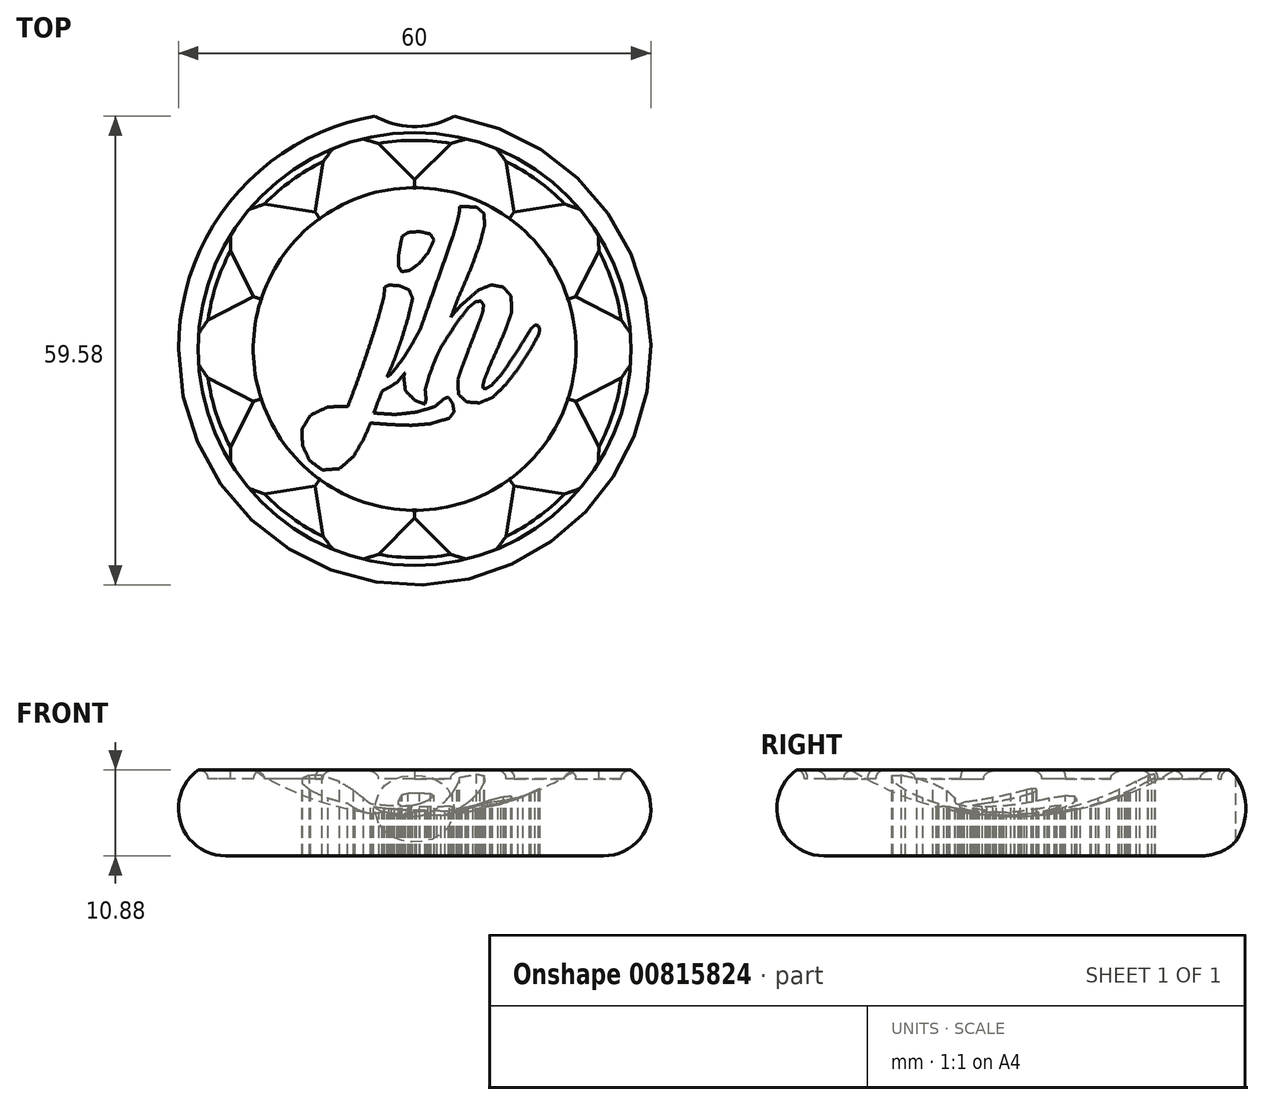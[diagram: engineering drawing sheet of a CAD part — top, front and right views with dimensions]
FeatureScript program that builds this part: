
annotation { "Feature Type Name" : "Feature", "Feature Type Description" : "" }
export const myFeature = defineFeature(function(context is Context, id is Id, definition is map)
    precondition{}
    {
        {
            var Q0;
            Q0=qCreatedBy(makeId("Front.planeOp"),FACE);
            var sketch = newSketch(context, id + "F0", { "sketchPlane" : qUnion([Q0])});
            skArc(sketch, "E0", {"start": v(-27.5, 16.42) * mm, "mid": v(-29.71, 9.7) * mm, "end": v(-24, 5.54) * mm});
            skArc(sketch, "E1", {"start": v(-20.5, 16.42) * mm, "mid": v(-10.66, 12.03) * mm, "end": v(0, 10.54) * mm});
            skLineSegment(sketch, "E2", {"start": v(-24, 5.54) * mm, "end": v(0, 5.54) * mm});
            skLineSegment(sketch, "E3", {"start": v(0, 5.54) * mm, "end": v(0, 10.54) * mm});
            skLineSegment(sketch, "E4.top", {"start": v(-27.5, 16.42) * mm, "end": v(-20.5, 16.42) * mm});
            skSolve(sketch);
        }
        {
            var Q0;
            Q0=makeQuery(id+"F0.imprint","IMPRINT",FACE,{"disambiguationData":[TD([[makeQuery(id+"F0.imprint","IMPRINT",EDGE,{"derivedFrom":sQuery(id+"F0.wireOp",EDGE,"E0")}),1.0]])]});
            var Q1;
            Q1=sQuery(id+"F0.wireOp",EDGE,"E3");
            revolve(context, id + "F1", {"surfaceOperationType" : NewSurfaceOperationType.NEW, "entities" : qUnion([Q0]), "axis" : qUnion([Q1]), "revolveType" : RevolveType.FULL});
        }
        {
            var Q0;
            Q0=qCreatedBy(makeId("Top.planeOp"),FACE);
            var Q1;
            Q1 = qBodyType(qCreatedBy(id + "F3" ,EDGE), BodyType.WIRE);
            cPlane(context, id + "F2", {"entities" : qUnion([Q0, Q1]), "cplaneType" : CPlaneType.OFFSET, "offset" : 25 * mm, "width" : 150 * mm, "height" : 150 * mm});
        }
        {
            var Q0;
            Q0=qCreatedBy(id+"F2.planeOp",FACE);
            var sketch = newSketch(context, id + "F3", { "sketchPlane" : qUnion([Q0])});
            skCircle(sketch, "E5", {"center": v(0, 0) * mm, "radius": 26.5 * mm});
            skCircle(sketch, "E6", {"center": v(0, 0) * mm, "radius": 21.5 * mm});
            skLineSegment(sketch, "E7", {"start": v(0, 21.5) * mm, "end": v(4.6, 26.1) * mm});
            skLineSegment(sketch, "E8.MirrorCS", {"start": v(0, 21.5) * mm, "end": v(-4.6, 26.1) * mm});
            skLineSegment(sketch, "E9.1.0", {"start": v(-12.64, 17.4) * mm, "end": v(-11.62, 23.82) * mm});
            skLineSegment(sketch, "E9.1.1", {"start": v(-12.64, 17.4) * mm, "end": v(-19.06, 18.41) * mm});
            skLineSegment(sketch, "E9.2.0", {"start": v(-20.45, 6.64) * mm, "end": v(-23.4, 12.44) * mm});
            skLineSegment(sketch, "E9.2.1", {"start": v(-20.45, 6.64) * mm, "end": v(-26.24, 3.7) * mm});
            skLineSegment(sketch, "E9.3.0", {"start": v(-20.45, -6.64) * mm, "end": v(-26.24, -3.7) * mm});
            skLineSegment(sketch, "E9.3.1", {"start": v(-20.45, -6.64) * mm, "end": v(-23.4, -12.44) * mm});
            skLineSegment(sketch, "E9.4.0", {"start": v(-12.64, -17.4) * mm, "end": v(-19.06, -18.41) * mm});
            skLineSegment(sketch, "E9.4.1", {"start": v(-12.64, -17.4) * mm, "end": v(-11.62, -23.82) * mm});
            skLineSegment(sketch, "E9.5.0", {"start": v(0, -21.5) * mm, "end": v(-4.6, -26.1) * mm});
            skLineSegment(sketch, "E9.5.1", {"start": v(0, -21.5) * mm, "end": v(4.6, -26.1) * mm});
            skLineSegment(sketch, "E9.6.0", {"start": v(12.64, -17.4) * mm, "end": v(11.62, -23.82) * mm});
            skLineSegment(sketch, "E9.6.1", {"start": v(12.64, -17.4) * mm, "end": v(19.06, -18.41) * mm});
            skLineSegment(sketch, "E9.7.0", {"start": v(20.45, -6.64) * mm, "end": v(23.4, -12.44) * mm});
            skLineSegment(sketch, "E9.7.1", {"start": v(20.45, -6.64) * mm, "end": v(26.24, -3.7) * mm});
            skLineSegment(sketch, "E9.8.0", {"start": v(20.45, 6.64) * mm, "end": v(26.24, 3.7) * mm});
            skLineSegment(sketch, "E9.8.1", {"start": v(20.45, 6.64) * mm, "end": v(23.4, 12.44) * mm});
            skLineSegment(sketch, "E9.9.0", {"start": v(12.64, 17.4) * mm, "end": v(19.06, 18.41) * mm});
            skLineSegment(sketch, "E9.9.1", {"start": v(12.64, 17.4) * mm, "end": v(11.62, 23.82) * mm});
            skSolve(sketch);
        }
        {
            var Q0;
            {var subQ0=sQuery(id+"F3.wireOp",EDGE,"E9.1.0");Q0=makeQuery(id+"F3.imprint","IMPRINT",FACE,{"disambiguationData":[TD([[makeQuery(id+"F3.imprint","IMPRINT",EDGE,{"derivedFrom":subQ0}),1.0]])]});}
            var Q1;
            {var subQ0=sQuery(id+"F3.wireOp",EDGE,"E7");Q1=makeQuery(id+"F3.imprint","IMPRINT",FACE,{"disambiguationData":[TD([[makeQuery(id+"F3.imprint","IMPRINT",EDGE,{"derivedFrom":subQ0}),1.0]])]});}
            var Q2;
            {var subQ0=sQuery(id+"F3.wireOp",EDGE,"E9.9.0");Q2=makeQuery(id+"F3.imprint","IMPRINT",FACE,{"disambiguationData":[TD([[makeQuery(id+"F3.imprint","IMPRINT",EDGE,{"derivedFrom":subQ0}),1.0]])]});}
            var Q3;
            {var subQ0=sQuery(id+"F3.wireOp",EDGE,"E9.8.0");Q3=makeQuery(id+"F3.imprint","IMPRINT",FACE,{"disambiguationData":[TD([[makeQuery(id+"F3.imprint","IMPRINT",EDGE,{"derivedFrom":subQ0}),1.0]])]});}
            var Q4;
            {var subQ0=sQuery(id+"F3.wireOp",EDGE,"E9.7.0");Q4=makeQuery(id+"F3.imprint","IMPRINT",FACE,{"disambiguationData":[TD([[makeQuery(id+"F3.imprint","IMPRINT",EDGE,{"derivedFrom":subQ0}),1.0]])]});}
            var Q5;
            {var subQ0=sQuery(id+"F3.wireOp",EDGE,"E9.6.0");Q5=makeQuery(id+"F3.imprint","IMPRINT",FACE,{"disambiguationData":[TD([[makeQuery(id+"F3.imprint","IMPRINT",EDGE,{"derivedFrom":subQ0}),1.0]])]});}
            var Q6;
            {var subQ0=sQuery(id+"F3.wireOp",EDGE,"E9.5.0");Q6=makeQuery(id+"F3.imprint","IMPRINT",FACE,{"disambiguationData":[TD([[makeQuery(id+"F3.imprint","IMPRINT",EDGE,{"derivedFrom":subQ0}),1.0]])]});}
            var Q7;
            {var subQ0=sQuery(id+"F3.wireOp",EDGE,"E9.4.0");Q7=makeQuery(id+"F3.imprint","IMPRINT",FACE,{"disambiguationData":[TD([[makeQuery(id+"F3.imprint","IMPRINT",EDGE,{"derivedFrom":subQ0}),1.0]])]});}
            var Q8;
            {var subQ0=sQuery(id+"F3.wireOp",EDGE,"E9.3.0");Q8=makeQuery(id+"F3.imprint","IMPRINT",FACE,{"disambiguationData":[TD([[makeQuery(id+"F3.imprint","IMPRINT",EDGE,{"derivedFrom":subQ0}),1.0]])]});}
            var Q9;
            {var subQ0=sQuery(id+"F3.wireOp",EDGE,"E9.2.0");Q9=makeQuery(id+"F3.imprint","IMPRINT",FACE,{"disambiguationData":[TD([[makeQuery(id+"F3.imprint","IMPRINT",EDGE,{"derivedFrom":subQ0}),1.0]])]});}
            extrude(context, id + "F4", {"entities" : qUnion([Q0, Q1, Q2, Q3, Q4, Q5, Q6, Q7, Q8, Q9]), "operationType" : NewBodyOperationType.REMOVE, "oppositeDirection" : true, "depth" : 9.7 * mm, "offsetDistance" : 25 * mm});
        }
        {
            var Q0;
            Q0=qCreatedBy(makeId("Top.planeOp"),FACE);
            var sketch = newSketch(context, id + "F5", { "sketchPlane" : qUnion([Q0])});
            skCircle(sketch, "E10", {"center": v(0, 38.24) * mm, "radius": 10 * mm});
            skSolve(sketch);
        }
        {
            var Q0;
            Q0=makeQuery(id+"F5.imprint","IMPRINT",FACE,{"disambiguationData":[TD([[makeQuery(id+"F5.imprint","IMPRINT",EDGE,{"derivedFrom":sQuery(id+"F5.wireOp",EDGE,"E10")}),1.0]])]});
            extrude(context, id + "F6", {"entities" : qUnion([Q0]), "operationType" : NewBodyOperationType.REMOVE, "depth" : 51 * mm, "offsetDistance" : 25 * mm});
        }
        {
            var Q0;
            Q0=qCreatedBy(id+"F2.planeOp",FACE);
            cPlane(context, id + "F7", {"entities" : qUnion([Q0]), "cplaneType" : CPlaneType.OFFSET, "offset" : 25 * mm, "width" : 150 * mm, "height" : 150 * mm});
        }
        {
            var Q0;
            Q0=qCreatedBy(id+"F7.planeOp",FACE);
            var sketch = newSketch(context, id + "F8", { "sketchPlane" : qUnion([Q0])});
            skLineSegment(sketch, "E11", {"start": v(-0.26, 6.42) * mm, "end": v(-0.82, 4) * mm});
            skLineSegment(sketch, "E12", {"start": v(-0.82, 4) * mm, "end": v(-1.68, 1.15) * mm});
            skLineSegment(sketch, "E13", {"start": v(-1.68, 1.15) * mm, "end": v(-2.63, -1.54) * mm});
            skLineSegment(sketch, "E14", {"start": v(-2.63, -1.54) * mm, "end": v(-3.47, -3.48) * mm});
            skLineSegment(sketch, "E15", {"start": v(-3.47, -3.48) * mm, "end": v(-3.1, -3.3) * mm});
            skLineSegment(sketch, "E16", {"start": v(-3.1, -3.3) * mm, "end": v(-2.7, -2.85) * mm});
            skLineSegment(sketch, "E17", {"start": v(-2.7, -2.85) * mm, "end": v(-1.4, -1.1) * mm});
            skLineSegment(sketch, "E18", {"start": v(-1.4, -1.1) * mm, "end": v(-0.26, 0.72) * mm});
            skLineSegment(sketch, "E19", {"start": v(-0.26, 0.72) * mm, "end": v(0.64, 2.37) * mm});
            skLineSegment(sketch, "E20", {"start": v(0.64, 2.37) * mm, "end": v(1.28, 3.62) * mm});
            skLineSegment(sketch, "E21", {"start": v(1.28, 3.62) * mm, "end": v(1.84, 4.39) * mm});
            skLineSegment(sketch, "E22", {"start": v(1.84, 4.39) * mm, "end": v(2.32, 4.39) * mm});
            skLineSegment(sketch, "E23", {"start": v(2.32, 4.39) * mm, "end": v(2.48, 3.73) * mm});
            skLineSegment(sketch, "E24", {"start": v(2.48, 3.73) * mm, "end": v(2.14, 2.58) * mm});
            skLineSegment(sketch, "E25", {"start": v(2.14, 2.58) * mm, "end": v(1, 0.38) * mm});
            skLineSegment(sketch, "E26", {"start": v(1, 0.38) * mm, "end": v(-0.49, -2.13) * mm});
            skLineSegment(sketch, "E27", {"start": v(-0.49, -2.13) * mm, "end": v(-2.25, -4.27) * mm});
            skLineSegment(sketch, "E28", {"start": v(-2.25, -4.27) * mm, "end": v(-4.15, -5.38) * mm});
            skLineSegment(sketch, "E29", {"start": v(-4.15, -5.38) * mm, "end": v(-5.19, -8.14) * mm});
            skLineSegment(sketch, "E30", {"start": v(-5.19, -8.14) * mm, "end": v(-2.52, -8.32) * mm});
            skLineSegment(sketch, "E31", {"start": v(-2.52, -8.32) * mm, "end": v(0.24, -8.03) * mm});
            skLineSegment(sketch, "E32", {"start": v(0.24, -8.03) * mm, "end": v(2.54, -7.33) * mm});
            skLineSegment(sketch, "E33", {"start": v(2.54, -7.33) * mm, "end": v(3.85, -6.24) * mm});
            skLineSegment(sketch, "E34", {"start": v(3.85, -6.24) * mm, "end": v(4.3, -6.15) * mm});
            skLineSegment(sketch, "E35", {"start": v(4.3, -6.15) * mm, "end": v(4.83, -6.92) * mm});
            skLineSegment(sketch, "E36", {"start": v(4.83, -6.92) * mm, "end": v(5, -7.98) * mm});
            skLineSegment(sketch, "E37", {"start": v(5, -7.98) * mm, "end": v(4.44, -8.77) * mm});
            skLineSegment(sketch, "E38", {"start": v(4.44, -8.77) * mm, "end": v(2.07, -9.5) * mm});
            skLineSegment(sketch, "E39", {"start": v(2.07, -9.5) * mm, "end": v(-0.4, -9.7) * mm});
            skLineSegment(sketch, "E40", {"start": v(-0.4, -9.7) * mm, "end": v(-2.95, -9.6) * mm});
            skLineSegment(sketch, "E41", {"start": v(-2.95, -9.6) * mm, "end": v(-5.6, -9.4) * mm});
            skLineSegment(sketch, "E42", {"start": v(-5.6, -9.4) * mm, "end": v(-6.45, -11.42) * mm});
            skLineSegment(sketch, "E43", {"start": v(-6.45, -11.42) * mm, "end": v(-7.77, -13.63) * mm});
            skLineSegment(sketch, "E44", {"start": v(-7.77, -13.63) * mm, "end": v(-9.53, -15.22) * mm});
            skLineSegment(sketch, "E45", {"start": v(-9.53, -15.22) * mm, "end": v(-11.74, -15.37) * mm});
            skLineSegment(sketch, "E46", {"start": v(-11.74, -15.37) * mm, "end": v(-13.35, -14.15) * mm});
            skLineSegment(sketch, "E47", {"start": v(-13.35, -14.15) * mm, "end": v(-14.25, -12.2) * mm});
            skLineSegment(sketch, "E48", {"start": v(-14.25, -12.2) * mm, "end": v(-14.28, -10.13) * mm});
            skLineSegment(sketch, "E49", {"start": v(-14.28, -10.13) * mm, "end": v(-13.24, -8.41) * mm});
            skLineSegment(sketch, "E50", {"start": v(-13.24, -8.41) * mm, "end": v(-11, -7.35) * mm});
            skLineSegment(sketch, "E51", {"start": v(-11, -7.35) * mm, "end": v(-8.49, -7.33) * mm});
            skLineSegment(sketch, "E52", {"start": v(-8.49, -7.33) * mm, "end": v(-7.54, -4.82) * mm});
            skLineSegment(sketch, "E53", {"start": v(-7.54, -4.82) * mm, "end": v(-6.45, -1.74) * mm});
            skLineSegment(sketch, "E54", {"start": v(-6.45, -1.74) * mm, "end": v(-5.4, 1.47) * mm});
            skLineSegment(sketch, "E55", {"start": v(-5.4, 1.47) * mm, "end": v(-4.49, 4.4) * mm});
            skLineSegment(sketch, "E56", {"start": v(-4.49, 4.4) * mm, "end": v(-3.9, 6.67) * mm});
            skLineSegment(sketch, "E57", {"start": v(-3.9, 6.67) * mm, "end": v(-3.79, 7.87) * mm});
            skLineSegment(sketch, "E58", {"start": v(-3.79, 7.87) * mm, "end": v(-3.27, 8.12) * mm});
            skLineSegment(sketch, "E59", {"start": v(-3.27, 8.12) * mm, "end": v(-1.96, 8.05) * mm});
            skLineSegment(sketch, "E60", {"start": v(-1.96, 8.05) * mm, "end": v(-0.69, 7.5) * mm});
            skLineSegment(sketch, "E61", {"start": v(-0.69, 7.5) * mm, "end": v(-0.26, 6.42) * mm});
            skLineSegment(sketch, "E62", {"start": v(-12.2, -9.22) * mm, "end": v(-12.97, -10.6) * mm});
            skLineSegment(sketch, "E63", {"start": v(-12.97, -10.6) * mm, "end": v(-12.97, -11.87) * mm});
            skLineSegment(sketch, "E64", {"start": v(-12.97, -11.87) * mm, "end": v(-12.54, -12.8) * mm});
            skLineSegment(sketch, "E65", {"start": v(-12.54, -12.8) * mm, "end": v(-11.97, -13.2) * mm});
            skLineSegment(sketch, "E66", {"start": v(-11.97, -13.2) * mm, "end": v(-11.5, -13.23) * mm});
            skLineSegment(sketch, "E67", {"start": v(-11.5, -13.23) * mm, "end": v(-10.9, -12.8) * mm});
            skLineSegment(sketch, "E68", {"start": v(-10.9, -12.8) * mm, "end": v(-10.1, -11.42) * mm});
            skLineSegment(sketch, "E69", {"start": v(-10.1, -11.42) * mm, "end": v(-8.94, -8.55) * mm});
            skLineSegment(sketch, "E70", {"start": v(-8.94, -8.55) * mm, "end": v(-11, -8.6) * mm});
            skLineSegment(sketch, "E71", {"start": v(-11, -8.6) * mm, "end": v(-12.2, -9.22) * mm});
            skLineSegment(sketch, "E72", {"start": v(-1.57, 14.33) * mm, "end": v(-0.8, 14.8) * mm});
            skLineSegment(sketch, "E73", {"start": v(-0.8, 14.8) * mm, "end": v(0.64, 14.92) * mm});
            skLineSegment(sketch, "E74", {"start": v(0.64, 14.92) * mm, "end": v(2, 14.6) * mm});
            skLineSegment(sketch, "E75", {"start": v(2, 14.6) * mm, "end": v(2.45, 13.84) * mm});
            skLineSegment(sketch, "E76", {"start": v(2.45, 13.84) * mm, "end": v(1.73, 12.25) * mm});
            skLineSegment(sketch, "E77", {"start": v(1.73, 12.25) * mm, "end": v(0.62, 10.9) * mm});
            skLineSegment(sketch, "E78", {"start": v(0.62, 10.9) * mm, "end": v(-0.6, 10) * mm});
            skLineSegment(sketch, "E79", {"start": v(-0.6, 10) * mm, "end": v(-1.66, 9.81) * mm});
            skLineSegment(sketch, "E80", {"start": v(-1.66, 9.81) * mm, "end": v(-2.07, 10.54) * mm});
            skLineSegment(sketch, "E81", {"start": v(-2.07, 10.54) * mm, "end": v(-2.02, 11.94) * mm});
            skLineSegment(sketch, "E82", {"start": v(-2.02, 11.94) * mm, "end": v(-1.77, 13.4) * mm});
            skLineSegment(sketch, "E83", {"start": v(-1.77, 13.4) * mm, "end": v(-1.57, 14.33) * mm});
            skLineSegment(sketch, "E84", {"start": v(8.33, 13.52) * mm, "end": v(7.4, 10.87) * mm});
            skLineSegment(sketch, "E85", {"start": v(7.4, 10.87) * mm, "end": v(6.45, 8.57) * mm});
            skLineSegment(sketch, "E86", {"start": v(6.45, 8.57) * mm, "end": v(5.5, 6.38) * mm});
            skLineSegment(sketch, "E87", {"start": v(5.5, 6.38) * mm, "end": v(4.62, 4.07) * mm});
            skLineSegment(sketch, "E88", {"start": v(4.62, 4.07) * mm, "end": v(5.78, 5.45) * mm});
            skLineSegment(sketch, "E89", {"start": v(5.78, 5.45) * mm, "end": v(8.15, 7.5) * mm});
            skLineSegment(sketch, "E90", {"start": v(8.15, 7.5) * mm, "end": v(9.73, 8.14) * mm});
            skLineSegment(sketch, "E91", {"start": v(9.73, 8.14) * mm, "end": v(11.27, 7.87) * mm});
            skLineSegment(sketch, "E92", {"start": v(11.27, 7.87) * mm, "end": v(12.26, 6.7) * mm});
            skLineSegment(sketch, "E93", {"start": v(12.26, 6.7) * mm, "end": v(12.3, 4.66) * mm});
            skLineSegment(sketch, "E94", {"start": v(12.3, 4.66) * mm, "end": v(11.6, 2.58) * mm});
            skLineSegment(sketch, "E95", {"start": v(11.6, 2.58) * mm, "end": v(10.6, 0.2) * mm});
            skLineSegment(sketch, "E96", {"start": v(10.6, 0.2) * mm, "end": v(9.57, -2.08) * mm});
            skLineSegment(sketch, "E97", {"start": v(9.57, -2.08) * mm, "end": v(8.87, -3.84) * mm});
            skLineSegment(sketch, "E98", {"start": v(8.87, -3.84) * mm, "end": v(8.7, -4.52) * mm});
            skLineSegment(sketch, "E99", {"start": v(8.7, -4.52) * mm, "end": v(8.71, -4.97) * mm});
            skLineSegment(sketch, "E100", {"start": v(8.71, -4.97) * mm, "end": v(9.03, -5.06) * mm});
            skLineSegment(sketch, "E101", {"start": v(9.03, -5.06) * mm, "end": v(9.78, -4.61) * mm});
            skLineSegment(sketch, "E102", {"start": v(9.78, -4.61) * mm, "end": v(10.95, -3.3) * mm});
            skLineSegment(sketch, "E103", {"start": v(10.95, -3.3) * mm, "end": v(12.4, -1.24) * mm});
            skLineSegment(sketch, "E104", {"start": v(12.4, -1.24) * mm, "end": v(13.78, 0.93) * mm});
            skLineSegment(sketch, "E105", {"start": v(13.78, 0.93) * mm, "end": v(14.8, 2.58) * mm});
            skLineSegment(sketch, "E106", {"start": v(14.8, 2.58) * mm, "end": v(15.32, 3.05) * mm});
            skLineSegment(sketch, "E107", {"start": v(15.32, 3.05) * mm, "end": v(15.72, 2.96) * mm});
            skLineSegment(sketch, "E108", {"start": v(15.72, 2.96) * mm, "end": v(15.9, 2.49) * mm});
            skLineSegment(sketch, "E109", {"start": v(15.9, 2.49) * mm, "end": v(15.75, 1.8) * mm});
            skLineSegment(sketch, "E110", {"start": v(15.75, 1.8) * mm, "end": v(14.62, -0.25) * mm});
            skLineSegment(sketch, "E111", {"start": v(14.62, -0.25) * mm, "end": v(13.15, -2.5) * mm});
            skLineSegment(sketch, "E112", {"start": v(13.15, -2.5) * mm, "end": v(11.52, -4.59) * mm});
            skLineSegment(sketch, "E113", {"start": v(11.52, -4.59) * mm, "end": v(9.91, -6.15) * mm});
            skLineSegment(sketch, "E114", {"start": v(9.91, -6.15) * mm, "end": v(8.24, -6.85) * mm});
            skLineSegment(sketch, "E115", {"start": v(8.24, -6.85) * mm, "end": v(6.64, -6.74) * mm});
            skLineSegment(sketch, "E116", {"start": v(6.64, -6.74) * mm, "end": v(5.57, -5.76) * mm});
            skLineSegment(sketch, "E117", {"start": v(5.57, -5.76) * mm, "end": v(5.48, -3.89) * mm});
            skLineSegment(sketch, "E118", {"start": v(5.48, -3.89) * mm, "end": v(6, -2.37) * mm});
            skLineSegment(sketch, "E119", {"start": v(6, -2.37) * mm, "end": v(6.88, -0.02) * mm});
            skLineSegment(sketch, "E120", {"start": v(6.88, -0.02) * mm, "end": v(7.88, 2.55) * mm});
            skLineSegment(sketch, "E121", {"start": v(7.88, 2.55) * mm, "end": v(8.65, 4.66) * mm});
            skLineSegment(sketch, "E122", {"start": v(8.65, 4.66) * mm, "end": v(8.76, 5.6) * mm});
            skLineSegment(sketch, "E123", {"start": v(8.76, 5.6) * mm, "end": v(8.42, 6.08) * mm});
            skLineSegment(sketch, "E124", {"start": v(8.42, 6.08) * mm, "end": v(7.74, 6.01) * mm});
            skLineSegment(sketch, "E125", {"start": v(7.74, 6.01) * mm, "end": v(6.88, 5.3) * mm});
            skLineSegment(sketch, "E126", {"start": v(6.88, 5.3) * mm, "end": v(5.32, 3.3) * mm});
            skLineSegment(sketch, "E127", {"start": v(5.32, 3.3) * mm, "end": v(3.36, 0.23) * mm});
            skLineSegment(sketch, "E128", {"start": v(3.36, 0.23) * mm, "end": v(2.84, -0.84) * mm});
            skLineSegment(sketch, "E129", {"start": v(2.84, -0.84) * mm, "end": v(1.86, -3.35) * mm});
            skLineSegment(sketch, "E130", {"start": v(1.86, -3.35) * mm, "end": v(1.34, -5.18) * mm});
            skLineSegment(sketch, "E131", {"start": v(1.34, -5.18) * mm, "end": v(1.46, -6.42) * mm});
            skLineSegment(sketch, "E132", {"start": v(1.46, -6.42) * mm, "end": v(1.3, -7) * mm});
            skLineSegment(sketch, "E133", {"start": v(1.3, -7) * mm, "end": v(0.08, -6.56) * mm});
            skLineSegment(sketch, "E134", {"start": v(0.08, -6.56) * mm, "end": v(-1.16, -5.31) * mm});
            skLineSegment(sketch, "E135", {"start": v(-1.16, -5.31) * mm, "end": v(-1.4, -3.48) * mm});
            skLineSegment(sketch, "E136", {"start": v(-1.4, -3.48) * mm, "end": v(1.68, 5.3) * mm});
            skLineSegment(sketch, "E137", {"start": v(1.68, 5.3) * mm, "end": v(4.85, 14.24) * mm});
            skLineSegment(sketch, "E138", {"start": v(4.85, 14.24) * mm, "end": v(5.4, 16.12) * mm});
            skLineSegment(sketch, "E139", {"start": v(5.4, 16.12) * mm, "end": v(5.64, 17.14) * mm});
            skLineSegment(sketch, "E140", {"start": v(5.64, 17.14) * mm, "end": v(5.7, 17.68) * mm});
            skLineSegment(sketch, "E141", {"start": v(5.7, 17.68) * mm, "end": v(5.7, 18.09) * mm});
            skLineSegment(sketch, "E142", {"start": v(5.7, 18.09) * mm, "end": v(7.86, 18.04) * mm});
            skLineSegment(sketch, "E143", {"start": v(7.86, 18.04) * mm, "end": v(8.83, 17.2) * mm});
            skLineSegment(sketch, "E144", {"start": v(8.83, 17.2) * mm, "end": v(8.87, 15.67) * mm});
            skLineSegment(sketch, "E145", {"start": v(8.87, 15.67) * mm, "end": v(8.33, 13.52) * mm});
            skSolve(sketch);
        }
        {
            var Q0;
            Q0=makeQuery(id+"F8.imprint","IMPRINT",FACE,{"disambiguationData":[TD([[makeQuery(id+"F8.imprint","IMPRINT",EDGE,{"derivedFrom":sQuery(id+"F8.wireOp",EDGE,"E11")}),-1.0]])]});
            var Q1;
            Q1=makeQuery(id+"F8.imprint","IMPRINT",FACE,{"disambiguationData":[TD([[makeQuery(id+"F8.imprint","IMPRINT",EDGE,{"derivedFrom":sQuery(id+"F8.wireOp",EDGE,"E72")}),-1.0]])]});
            var Q2;
            {var subQ4=sQuery(id+"F8.wireOp",EDGE,"E21");Q2=makeQuery(id+"F8.imprint","IMPRINT",FACE,{"disambiguationData":[TD([[makeQuery(id+"F8.imprint","IMPRINT",EDGE,{"derivedFrom":subQ4}),1.0]])]});}
            var Q3;
            Q3=makeQuery(id+"F8.imprint","IMPRINT",FACE,{"disambiguationData":[TD([[makeQuery(id+"F8.imprint","IMPRINT",EDGE,{"derivedFrom":sQuery(id+"F8.wireOp",EDGE,"E62")}),1.0]])]});
            var Q4;
            {var subQ0=sQuery(id+"F8.wireOp",EDGE,"E21");Q4=makeQuery(id+"F8.imprint","IMPRINT",FACE,{"disambiguationData":[TD([[makeQuery(id+"F8.imprint","IMPRINT",EDGE,{"derivedFrom":subQ0}),-1.0]])]});}
            extrude(context, id + "F9", {"entities" : qUnion([Q0, Q1, Q2, Q3, Q4]), "operationType" : NewBodyOperationType.REMOVE, "oppositeDirection" : true, "depth" : 60 * mm, "offsetDistance" : 25 * mm});
        }
        {
            var Q0;
            {var subQ0=sQuery(id+"F3.wireOp",EDGE,"E5");Q0=makeQuery(id+"F4.boolean.opBoolean","INTERSECT",EDGE,{"derivedFrom":[makeQuery(id+"F1.opRevolve","SWEPT_FACE",FACE,{"disambiguationData":[OSD([sQuery(id+"F0.wireOp",EDGE,"E4.top")])]}),makeQuery(id+"F4.opExtrude","SWEPT_FACE",FACE,{"disambiguationData":[OSD([subQ0]),TDD([makeQuery(id+"F3.imprint","IMPRINT",EDGE,{"disambiguationData":[TD([[makeQuery(id+"F3.imprint","INTERSECT",VERTEX,{"derivedFrom":[subQ0,sQuery(id+"F3.wireOp",EDGE,"E9.1.0")]}),-1.0]])],"derivedFrom":subQ0})])]})]});}
            var Q1;
            Q1=makeQuery(id+"F4.boolean.opBoolean","INTERSECT",EDGE,{"derivedFrom":[makeQuery(id+"F1.opRevolve","SWEPT_FACE",FACE,{"disambiguationData":[OSD([sQuery(id+"F0.wireOp",EDGE,"E4.top")])]}),makeQuery(id+"F4.opExtrude","SWEPT_FACE",FACE,{"disambiguationData":[OSD([sQuery(id+"F3.wireOp",EDGE,"E9.1.0")])]})]});
            var Q2;
            Q2=makeQuery(id+"F4.boolean.opBoolean","INTERSECT",EDGE,{"derivedFrom":[makeQuery(id+"F1.opRevolve","SWEPT_FACE",FACE,{"disambiguationData":[OSD([sQuery(id+"F0.wireOp",EDGE,"E4.top")])]}),makeQuery(id+"F4.opExtrude","SWEPT_FACE",FACE,{"disambiguationData":[OSD([sQuery(id+"F3.wireOp",EDGE,"E9.1.1")])]})]});
            var Q3;
            Q3=makeQuery(id+"F4.boolean.opBoolean","INTERSECT",EDGE,{"derivedFrom":[makeQuery(id+"F1.opRevolve","SWEPT_FACE",FACE,{"disambiguationData":[OSD([sQuery(id+"F0.wireOp",EDGE,"E4.top")])]}),makeQuery(id+"F4.opExtrude","SWEPT_FACE",FACE,{"disambiguationData":[OSD([sQuery(id+"F3.wireOp",EDGE,"E9.2.0")])]})]});
            var Q4;
            {var subQ0=sQuery(id+"F3.wireOp",EDGE,"E5");Q4=makeQuery(id+"F4.boolean.opBoolean","INTERSECT",EDGE,{"derivedFrom":[makeQuery(id+"F1.opRevolve","SWEPT_FACE",FACE,{"disambiguationData":[OSD([sQuery(id+"F0.wireOp",EDGE,"E4.top")])]}),makeQuery(id+"F4.opExtrude","SWEPT_FACE",FACE,{"disambiguationData":[OSD([subQ0]),TDD([makeQuery(id+"F3.imprint","IMPRINT",EDGE,{"disambiguationData":[TD([[makeQuery(id+"F3.imprint","INTERSECT",VERTEX,{"derivedFrom":[subQ0,sQuery(id+"F3.wireOp",EDGE,"E9.2.0")]}),-1.0]])],"derivedFrom":subQ0})])]})]});}
            var Q5;
            Q5=makeQuery(id+"F4.boolean.opBoolean","INTERSECT",EDGE,{"derivedFrom":[makeQuery(id+"F1.opRevolve","SWEPT_FACE",FACE,{"disambiguationData":[OSD([sQuery(id+"F0.wireOp",EDGE,"E4.top")])]}),makeQuery(id+"F4.opExtrude","SWEPT_FACE",FACE,{"disambiguationData":[OSD([sQuery(id+"F3.wireOp",EDGE,"E9.2.1")])]})]});
            var Q6;
            Q6=makeQuery(id+"F4.boolean.opBoolean","INTERSECT",EDGE,{"derivedFrom":[makeQuery(id+"F1.opRevolve","SWEPT_FACE",FACE,{"disambiguationData":[OSD([sQuery(id+"F0.wireOp",EDGE,"E4.top")])]}),makeQuery(id+"F4.opExtrude","SWEPT_FACE",FACE,{"disambiguationData":[OSD([sQuery(id+"F3.wireOp",EDGE,"E9.3.0")])]})]});
            var Q7;
            {var subQ0=sQuery(id+"F3.wireOp",EDGE,"E5");Q7=makeQuery(id+"F4.boolean.opBoolean","INTERSECT",EDGE,{"derivedFrom":[makeQuery(id+"F1.opRevolve","SWEPT_FACE",FACE,{"disambiguationData":[OSD([sQuery(id+"F0.wireOp",EDGE,"E4.top")])]}),makeQuery(id+"F4.opExtrude","SWEPT_FACE",FACE,{"disambiguationData":[OSD([subQ0]),TDD([makeQuery(id+"F3.imprint","IMPRINT",EDGE,{"disambiguationData":[TD([[makeQuery(id+"F3.imprint","INTERSECT",VERTEX,{"derivedFrom":[subQ0,sQuery(id+"F3.wireOp",EDGE,"E9.3.0")]}),-1.0]])],"derivedFrom":subQ0})])]})]});}
            var Q8;
            Q8=makeQuery(id+"F4.boolean.opBoolean","INTERSECT",EDGE,{"derivedFrom":[makeQuery(id+"F1.opRevolve","SWEPT_FACE",FACE,{"disambiguationData":[OSD([sQuery(id+"F0.wireOp",EDGE,"E4.top")])]}),makeQuery(id+"F4.opExtrude","SWEPT_FACE",FACE,{"disambiguationData":[OSD([sQuery(id+"F3.wireOp",EDGE,"E9.3.1")])]})]});
            var Q9;
            Q9=makeQuery(id+"F4.boolean.opBoolean","INTERSECT",EDGE,{"derivedFrom":[makeQuery(id+"F1.opRevolve","SWEPT_FACE",FACE,{"disambiguationData":[OSD([sQuery(id+"F0.wireOp",EDGE,"E4.top")])]}),makeQuery(id+"F4.opExtrude","SWEPT_FACE",FACE,{"disambiguationData":[OSD([sQuery(id+"F3.wireOp",EDGE,"E9.4.0")])]})]});
            var Q10;
            {var subQ0=sQuery(id+"F3.wireOp",EDGE,"E5");Q10=makeQuery(id+"F4.boolean.opBoolean","INTERSECT",EDGE,{"derivedFrom":[makeQuery(id+"F1.opRevolve","SWEPT_FACE",FACE,{"disambiguationData":[OSD([sQuery(id+"F0.wireOp",EDGE,"E4.top")])]}),makeQuery(id+"F4.opExtrude","SWEPT_FACE",FACE,{"disambiguationData":[OSD([subQ0]),TDD([makeQuery(id+"F3.imprint","IMPRINT",EDGE,{"disambiguationData":[TD([[makeQuery(id+"F3.imprint","INTERSECT",VERTEX,{"derivedFrom":[subQ0,sQuery(id+"F3.wireOp",EDGE,"E9.4.0")]}),-1.0]])],"derivedFrom":subQ0})])]})]});}
            var Q11;
            Q11=makeQuery(id+"F4.boolean.opBoolean","INTERSECT",EDGE,{"derivedFrom":[makeQuery(id+"F1.opRevolve","SWEPT_FACE",FACE,{"disambiguationData":[OSD([sQuery(id+"F0.wireOp",EDGE,"E4.top")])]}),makeQuery(id+"F4.opExtrude","SWEPT_FACE",FACE,{"disambiguationData":[OSD([sQuery(id+"F3.wireOp",EDGE,"E9.4.1")])]})]});
            var Q12;
            Q12=makeQuery(id+"F4.boolean.opBoolean","INTERSECT",EDGE,{"derivedFrom":[makeQuery(id+"F1.opRevolve","SWEPT_FACE",FACE,{"disambiguationData":[OSD([sQuery(id+"F0.wireOp",EDGE,"E4.top")])]}),makeQuery(id+"F4.opExtrude","SWEPT_FACE",FACE,{"disambiguationData":[OSD([sQuery(id+"F3.wireOp",EDGE,"E9.5.0")])]})]});
            var Q13;
            Q13=makeQuery(id+"F4.boolean.opBoolean","INTERSECT",EDGE,{"derivedFrom":[makeQuery(id+"F1.opRevolve","SWEPT_FACE",FACE,{"disambiguationData":[OSD([sQuery(id+"F0.wireOp",EDGE,"E4.top")])]}),makeQuery(id+"F4.opExtrude","SWEPT_FACE",FACE,{"disambiguationData":[OSD([sQuery(id+"F3.wireOp",EDGE,"E9.5.1")])]})]});
            var Q14;
            {var subQ0=sQuery(id+"F3.wireOp",EDGE,"E5");Q14=makeQuery(id+"F4.boolean.opBoolean","INTERSECT",EDGE,{"derivedFrom":[makeQuery(id+"F1.opRevolve","SWEPT_FACE",FACE,{"disambiguationData":[OSD([sQuery(id+"F0.wireOp",EDGE,"E4.top")])]}),makeQuery(id+"F4.opExtrude","SWEPT_FACE",FACE,{"disambiguationData":[OSD([subQ0]),TDD([makeQuery(id+"F3.imprint","IMPRINT",EDGE,{"disambiguationData":[TD([[makeQuery(id+"F3.imprint","INTERSECT",VERTEX,{"derivedFrom":[subQ0,sQuery(id+"F3.wireOp",EDGE,"E9.5.0")]}),-1.0]])],"derivedFrom":subQ0})])]})]});}
            var Q15;
            Q15=makeQuery(id+"F4.boolean.opBoolean","INTERSECT",EDGE,{"derivedFrom":[makeQuery(id+"F1.opRevolve","SWEPT_FACE",FACE,{"disambiguationData":[OSD([sQuery(id+"F0.wireOp",EDGE,"E4.top")])]}),makeQuery(id+"F4.opExtrude","SWEPT_FACE",FACE,{"disambiguationData":[OSD([sQuery(id+"F3.wireOp",EDGE,"E9.6.0")])]})]});
            var Q16;
            {var subQ0=sQuery(id+"F3.wireOp",EDGE,"E5");Q16=makeQuery(id+"F4.boolean.opBoolean","INTERSECT",EDGE,{"derivedFrom":[makeQuery(id+"F1.opRevolve","SWEPT_FACE",FACE,{"disambiguationData":[OSD([sQuery(id+"F0.wireOp",EDGE,"E4.top")])]}),makeQuery(id+"F4.opExtrude","SWEPT_FACE",FACE,{"disambiguationData":[OSD([subQ0]),TDD([makeQuery(id+"F3.imprint","IMPRINT",EDGE,{"disambiguationData":[TD([[makeQuery(id+"F3.imprint","INTERSECT",VERTEX,{"derivedFrom":[subQ0,sQuery(id+"F3.wireOp",EDGE,"E9.6.0")]}),-1.0]])],"derivedFrom":subQ0})])]})]});}
            var Q17;
            Q17=makeQuery(id+"F4.boolean.opBoolean","INTERSECT",EDGE,{"derivedFrom":[makeQuery(id+"F1.opRevolve","SWEPT_FACE",FACE,{"disambiguationData":[OSD([sQuery(id+"F0.wireOp",EDGE,"E4.top")])]}),makeQuery(id+"F4.opExtrude","SWEPT_FACE",FACE,{"disambiguationData":[OSD([sQuery(id+"F3.wireOp",EDGE,"E9.6.1")])]})]});
            var Q18;
            Q18=makeQuery(id+"F4.boolean.opBoolean","INTERSECT",EDGE,{"derivedFrom":[makeQuery(id+"F1.opRevolve","SWEPT_FACE",FACE,{"disambiguationData":[OSD([sQuery(id+"F0.wireOp",EDGE,"E4.top")])]}),makeQuery(id+"F4.opExtrude","SWEPT_FACE",FACE,{"disambiguationData":[OSD([sQuery(id+"F3.wireOp",EDGE,"E9.7.0")])]})]});
            var Q19;
            Q19=makeQuery(id+"F4.boolean.opBoolean","INTERSECT",EDGE,{"derivedFrom":[makeQuery(id+"F1.opRevolve","SWEPT_FACE",FACE,{"disambiguationData":[OSD([sQuery(id+"F0.wireOp",EDGE,"E4.top")])]}),makeQuery(id+"F4.opExtrude","SWEPT_FACE",FACE,{"disambiguationData":[OSD([sQuery(id+"F3.wireOp",EDGE,"E9.7.1")])]})]});
            var Q20;
            {var subQ0=sQuery(id+"F3.wireOp",EDGE,"E5");Q20=makeQuery(id+"F4.boolean.opBoolean","INTERSECT",EDGE,{"derivedFrom":[makeQuery(id+"F1.opRevolve","SWEPT_FACE",FACE,{"disambiguationData":[OSD([sQuery(id+"F0.wireOp",EDGE,"E4.top")])]}),makeQuery(id+"F4.opExtrude","SWEPT_FACE",FACE,{"disambiguationData":[OSD([subQ0]),TDD([makeQuery(id+"F3.imprint","IMPRINT",EDGE,{"disambiguationData":[TD([[makeQuery(id+"F3.imprint","INTERSECT",VERTEX,{"derivedFrom":[subQ0,sQuery(id+"F3.wireOp",EDGE,"E9.7.0")]}),-1.0]])],"derivedFrom":subQ0})])]})]});}
            var Q21;
            {var subQ0=sQuery(id+"F3.wireOp",EDGE,"E5");Q21=makeQuery(id+"F4.boolean.opBoolean","INTERSECT",EDGE,{"derivedFrom":[makeQuery(id+"F1.opRevolve","SWEPT_FACE",FACE,{"disambiguationData":[OSD([sQuery(id+"F0.wireOp",EDGE,"E4.top")])]}),makeQuery(id+"F4.opExtrude","SWEPT_FACE",FACE,{"disambiguationData":[OSD([subQ0]),TDD([makeQuery(id+"F3.imprint","IMPRINT",EDGE,{"disambiguationData":[TD([[makeQuery(id+"F3.imprint","INTERSECT",VERTEX,{"derivedFrom":[subQ0,sQuery(id+"F3.wireOp",EDGE,"E9.8.0")]}),-1.0]])],"derivedFrom":subQ0})])]})]});}
            var Q22;
            Q22=makeQuery(id+"F4.boolean.opBoolean","INTERSECT",EDGE,{"derivedFrom":[makeQuery(id+"F1.opRevolve","SWEPT_FACE",FACE,{"disambiguationData":[OSD([sQuery(id+"F0.wireOp",EDGE,"E4.top")])]}),makeQuery(id+"F4.opExtrude","SWEPT_FACE",FACE,{"disambiguationData":[OSD([sQuery(id+"F3.wireOp",EDGE,"E9.8.1")])]})]});
            var Q23;
            Q23=makeQuery(id+"F4.boolean.opBoolean","INTERSECT",EDGE,{"derivedFrom":[makeQuery(id+"F1.opRevolve","SWEPT_FACE",FACE,{"disambiguationData":[OSD([sQuery(id+"F0.wireOp",EDGE,"E4.top")])]}),makeQuery(id+"F4.opExtrude","SWEPT_FACE",FACE,{"disambiguationData":[OSD([sQuery(id+"F3.wireOp",EDGE,"E9.8.0")])]})]});
            var Q24;
            Q24=makeQuery(id+"F4.boolean.opBoolean","INTERSECT",EDGE,{"derivedFrom":[makeQuery(id+"F1.opRevolve","SWEPT_FACE",FACE,{"disambiguationData":[OSD([sQuery(id+"F0.wireOp",EDGE,"E4.top")])]}),makeQuery(id+"F4.opExtrude","SWEPT_FACE",FACE,{"disambiguationData":[OSD([sQuery(id+"F3.wireOp",EDGE,"E9.9.1")])]})]});
            var Q25;
            Q25=makeQuery(id+"F4.boolean.opBoolean","INTERSECT",EDGE,{"derivedFrom":[makeQuery(id+"F1.opRevolve","SWEPT_FACE",FACE,{"disambiguationData":[OSD([sQuery(id+"F0.wireOp",EDGE,"E4.top")])]}),makeQuery(id+"F4.opExtrude","SWEPT_FACE",FACE,{"disambiguationData":[OSD([sQuery(id+"F3.wireOp",EDGE,"E9.9.0")])]})]});
            var Q26;
            {var subQ0=sQuery(id+"F3.wireOp",EDGE,"E5");Q26=makeQuery(id+"F4.boolean.opBoolean","INTERSECT",EDGE,{"derivedFrom":[makeQuery(id+"F1.opRevolve","SWEPT_FACE",FACE,{"disambiguationData":[OSD([sQuery(id+"F0.wireOp",EDGE,"E4.top")])]}),makeQuery(id+"F4.opExtrude","SWEPT_FACE",FACE,{"disambiguationData":[OSD([subQ0]),TDD([makeQuery(id+"F3.imprint","IMPRINT",EDGE,{"disambiguationData":[TD([[makeQuery(id+"F3.imprint","INTERSECT",VERTEX,{"derivedFrom":[subQ0,sQuery(id+"F3.wireOp",EDGE,"E9.9.0")]}),-1.0]])],"derivedFrom":subQ0})])]})]});}
            var Q27;
            Q27=makeQuery(id+"F4.boolean.opBoolean","INTERSECT",EDGE,{"derivedFrom":[makeQuery(id+"F1.opRevolve","SWEPT_FACE",FACE,{"disambiguationData":[OSD([sQuery(id+"F0.wireOp",EDGE,"E4.top")])]}),makeQuery(id+"F4.opExtrude","SWEPT_FACE",FACE,{"disambiguationData":[OSD([sQuery(id+"F3.wireOp",EDGE,"E7")])]})]});
            var Q28;
            {var subQ0=sQuery(id+"F3.wireOp",EDGE,"E5");Q28=makeQuery(id+"F4.boolean.opBoolean","INTERSECT",EDGE,{"derivedFrom":[makeQuery(id+"F1.opRevolve","SWEPT_FACE",FACE,{"disambiguationData":[OSD([sQuery(id+"F0.wireOp",EDGE,"E4.top")])]}),makeQuery(id+"F4.opExtrude","SWEPT_FACE",FACE,{"disambiguationData":[OSD([subQ0]),TDD([makeQuery(id+"F3.imprint","IMPRINT",EDGE,{"disambiguationData":[TD([[makeQuery(id+"F3.imprint","INTERSECT",VERTEX,{"derivedFrom":[subQ0,sQuery(id+"F3.wireOp",EDGE,"E7")]}),-1.0]])],"derivedFrom":subQ0})])]})]});}
            var Q29;
            Q29=makeQuery(id+"F4.boolean.opBoolean","INTERSECT",EDGE,{"derivedFrom":[makeQuery(id+"F1.opRevolve","SWEPT_FACE",FACE,{"disambiguationData":[OSD([sQuery(id+"F0.wireOp",EDGE,"E4.top")])]}),makeQuery(id+"F4.opExtrude","SWEPT_FACE",FACE,{"disambiguationData":[OSD([sQuery(id+"F3.wireOp",EDGE,"E8.MirrorCS")])]})]});
            fillet(context, id + "F10", {"entities" : qUnion([Q0, Q1, Q2, Q3, Q4, Q5, Q6, Q7, Q8, Q9, Q10, Q11, Q12, Q13, Q14, Q15, Q16, Q17, Q18, Q19, Q20, Q21, Q22, Q23, Q24, Q25, Q26, Q27, Q28, Q29]), "radius" : 0.97 * mm, "tangentPropagation" : true, "allowEdgeOverflow" : false});
        }
    });
